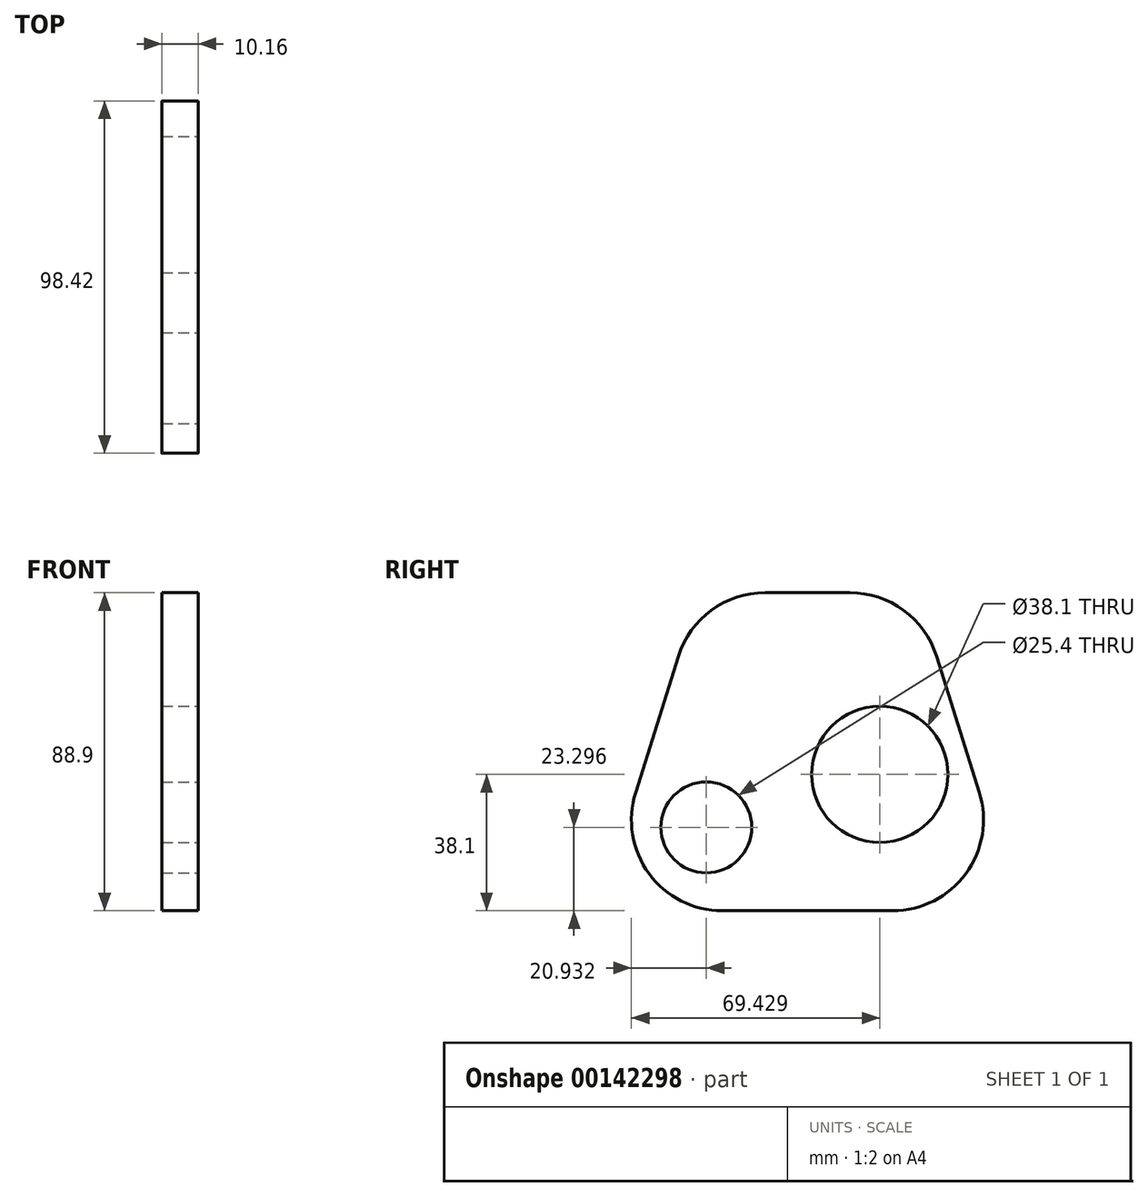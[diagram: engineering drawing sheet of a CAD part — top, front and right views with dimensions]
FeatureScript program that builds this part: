
annotation { "Feature Type Name" : "Feature", "Feature Type Description" : "" }
export const myFeature = defineFeature(function(context is Context, id is Id, definition is map)
    precondition{}
    {
        {
            var Q0;
            Q0=qCreatedBy(makeId("Right.planeOp"),FACE);
            var sketch = newSketch(context, id + "F0", { "sketchPlane" : qUnion([Q0])});
            skLineSegment(sketch, "E0", {"start": v(-30.48, 50.8) * mm, "end": v(30.48, 50.8) * mm});
            skLineSegment(sketch, "E1", {"start": v(30.48, 50.8) * mm, "end": v(58.42, -38.1) * mm});
            skLineSegment(sketch, "E2", {"start": v(58.42, -38.1) * mm, "end": v(-58.42, -38.1) * mm});
            skLineSegment(sketch, "E3", {"start": v(-58.42, -38.1) * mm, "end": v(-30.48, 50.8) * mm});
            skSolve(sketch);
        }
        {
            var Q0;
            Q0 = qSketchRegion(id + "F0", true);
            extrude(context, id + "F1", {"entities" : qUnion([Q0]), "depth" : 5.08 * mm, "hasSecondDirection" : true, "secondDirectionOppositeDirection" : true, "secondDirectionDepth" : 5.08 * mm});
        }
        {
            var Q0;
            Q0=makeQuery(id+"F1.opExtrude","SWEPT_EDGE",EDGE,{"disambiguationData":[OSD([sQuery(id+"F0.wireOp",EDGE,"E0"),sQuery(id+"F0.wireOp",EDGE,"E3")])]});
            var Q1;
            Q1=makeQuery(id+"F1.opExtrude","SWEPT_EDGE",EDGE,{"disambiguationData":[OSD([sQuery(id+"F0.wireOp",EDGE,"E2"),sQuery(id+"F0.wireOp",EDGE,"E3")])]});
            var Q2;
            Q2=makeQuery(id+"F1.opExtrude","SWEPT_EDGE",EDGE,{"disambiguationData":[OSD([sQuery(id+"F0.wireOp",EDGE,"E0"),sQuery(id+"F0.wireOp",EDGE,"E1")])]});
            var Q3;
            Q3=makeQuery(id+"F1.opExtrude","SWEPT_EDGE",EDGE,{"disambiguationData":[OSD([sQuery(id+"F0.wireOp",EDGE,"E1"),sQuery(id+"F0.wireOp",EDGE,"E2")])]});
            fillet(context, id + "F2", {"entities" : qUnion([Q0, Q1, Q2, Q3]), "radius" : 25.4 * mm, "tangentPropagation" : true, "allowEdgeOverflow" : false});
        }
        {
            var Q0;
            Q0=makeQuery(id+"F1.opExtrude","CAP_FACE",FACE,{"disambiguationData":[OSD([sQuery(id+"F0.wireOp",EDGE,"E0"),sQuery(id+"F0.wireOp",EDGE,"E1"),sQuery(id+"F0.wireOp",EDGE,"E2"),sQuery(id+"F0.wireOp",EDGE,"E3")])],"isStart":false});
            var sketch = newSketch(context, id + "F3", { "sketchPlane" : qUnion([Q0])});
            skCircle(sketch, "E4", {"center": v(20.22, 0) * mm, "radius": 19.05 * mm});
            skSolve(sketch);
        }
        {
            var Q0;
            Q0 = qSketchRegion(id + "F3", true);
            extrude(context, id + "F4", {"entities" : qUnion([Q0]), "operationType" : NewBodyOperationType.REMOVE, "oppositeDirection" : true, "depth" : 25.4 * mm});
        }
        {
            var Q0;
            Q0=makeQuery(id+"F1.opExtrude","CAP_FACE",FACE,{"disambiguationData":[OSD([sQuery(id+"F0.wireOp",EDGE,"E0"),sQuery(id+"F0.wireOp",EDGE,"E1"),sQuery(id+"F0.wireOp",EDGE,"E2"),sQuery(id+"F0.wireOp",EDGE,"E3")])],"isStart":false});
            var sketch = newSketch(context, id + "F5", { "sketchPlane" : qUnion([Q0])});
            skCircle(sketch, "E5", {"center": v(-28.28, -14.8) * mm, "radius": 12.7 * mm});
            skSolve(sketch);
        }
        {
            var Q0;
            Q0 = qSketchRegion(id + "F5", true);
            extrude(context, id + "F6", {"entities" : qUnion([Q0]), "operationType" : NewBodyOperationType.REMOVE, "oppositeDirection" : true, "depth" : 25.4 * mm});
        }
    });
